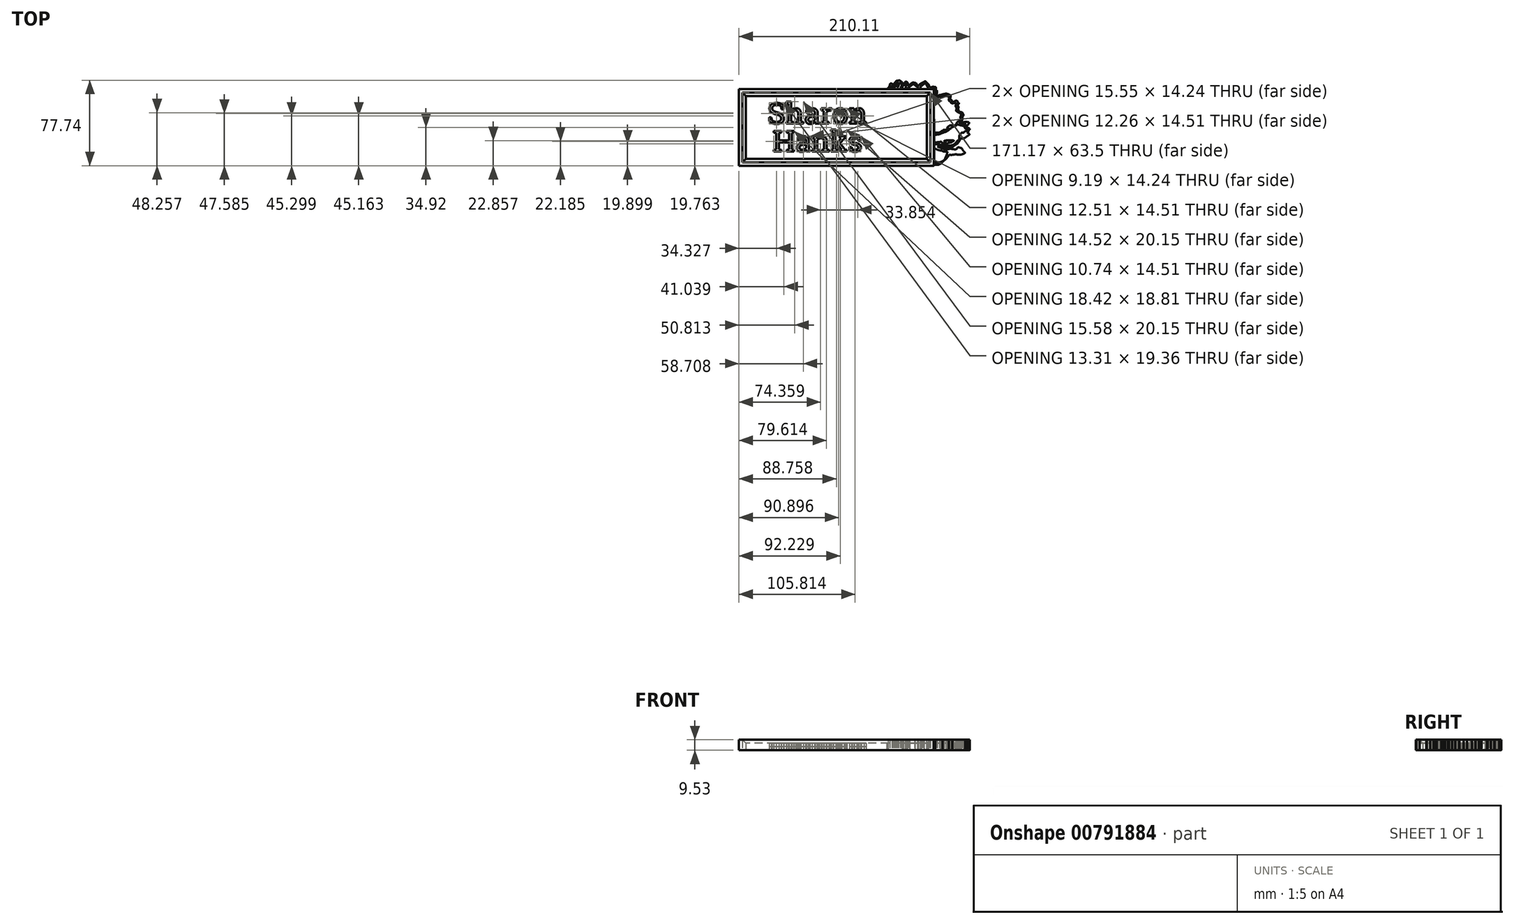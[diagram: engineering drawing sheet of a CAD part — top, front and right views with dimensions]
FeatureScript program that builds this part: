
annotation { "Feature Type Name" : "Feature", "Feature Type Description" : "" }
export const myFeature = defineFeature(function(context is Context, id is Id, definition is map)
    precondition{}
    {
        {
            var Q0;
            Q0=qCreatedBy(makeId("Top.planeOp"),FACE);
            var sketch = newSketch(context, id + "F0", { "sketchPlane" : qUnion([Q0])});
            skText(sketch, "E0", { "text": "Sharon", "fontName": "RobotoSlab-Regular.ttf"});
            skText(sketch, "E1", { "text": "Hanks", "fontName": "RobotoSlab-Regular.ttf"});
            skLineSegment(sketch, "E2.bottom", {"start": v(115.88, 31.75) * mm, "end": v(-55.29, 31.75) * mm});
            skLineSegment(sketch, "E2.top", {"start": v(115.88, -31.75) * mm, "end": v(-55.29, -31.75) * mm});
            skLineSegment(sketch, "E2.left", {"start": v(115.88, 31.75) * mm, "end": v(115.88, -31.75) * mm});
            skPoint(sketch, "E2.middle", {"position": v(0, 0.08) * mm});
            skLineSegment(sketch, "E3", {"start": v(-55.29, 31.75) * mm, "end": v(-55.29, -31.75) * mm});
            skPoint(sketch, "E2.right.start.orphan", {"position": v(-141.56, 31.75) * mm});
            skPoint(sketch, "E4.orphan", {"position": v(-141.56, -31.75) * mm});
            skLineSegment(sketch, "E5.0", {"start": v(112.7, 28.57) * mm, "end": v(-52.11, 28.57) * mm});
            skLineSegment(sketch, "E5.1", {"start": v(112.7, 28.57) * mm, "end": v(112.7, -28.58) * mm});
            skLineSegment(sketch, "E5.2", {"start": v(112.7, -28.57) * mm, "end": v(-52.11, -28.57) * mm});
            skLineSegment(sketch, "E5.3", {"start": v(-52.11, 28.57) * mm, "end": v(-52.11, -28.57) * mm});
            skLineSegment(sketch, "E6.0", {"start": v(-58.46, 34.92) * mm, "end": v(-58.46, -34.92) * mm});
            skLineSegment(sketch, "E6.1", {"start": v(119.06, 34.92) * mm, "end": v(-58.46, 34.92) * mm});
            skLineSegment(sketch, "E6.2", {"start": v(119.06, 34.92) * mm, "end": v(119.06, -34.93) * mm});
            skLineSegment(sketch, "E6.3", {"start": v(119.06, -34.92) * mm, "end": v(-58.46, -34.92) * mm});
            skLineSegment(sketch, "E7", {"start": v(13.4, 3.26) * mm, "end": v(13.4, -3.1) * mm, "construction": true});
            skLineSegment(sketch, "E8", {"start": v(0, 3.26) * mm, "end": v(0, 0.08) * mm, "construction": true});
            skLineSegment(sketch, "E9", {"start": v(0, 0.08) * mm, "end": v(0, -3.1) * mm, "construction": true});
            const initialGuessF0  = {"E0": [-0.03235, 0.00326, 1, 0, 0.01905], "E1": [-0.02755, -0.02214, 1, 0, 0.01905]};
            skSetInitialGuess(sketch, initialGuessF0);
            skSolve(sketch);
        }
        {
            var Q0;
            Q0=qCreatedBy(makeId("Top.planeOp"),FACE);
            var sketch = newSketch(context, id + "F1", { "sketchPlane" : qUnion([Q0])});
            skFitSpline(sketch, "E10", {"points": [v(133.1, 29.85) * mm, v(130.12, 30.6) * mm, v(127, 29.98) * mm, v(124.08, 29.3) * mm]});
            skFitSpline(sketch, "E11", {"points": [v(124.08, 29.3) * mm, v(122.27, 28.6) * mm, v(121.27, 26.77) * mm, v(120.02, 25.45) * mm]});
            skFitSpline(sketch, "E12", {"points": [v(120.02, 25.45) * mm, v(120.68, 28.13) * mm, v(121.7, 30.78) * mm, v(121.7, 33.57) * mm]});
            skFitSpline(sketch, "E13", {"points": [v(121.7, 33.57) * mm, v(120.84, 34.53) * mm, v(120.84, 36.36) * mm, v(119.43, 36.74) * mm]});
            skFitSpline(sketch, "E14", {"points": [v(119.43, 36.74) * mm, v(117.99, 36.9) * mm, v(116.43, 36.39) * mm, v(115.09, 36.42) * mm]});
            skFitSpline(sketch, "E15", {"points": [v(115.09, 36.42) * mm, v(114.61, 38.18) * mm, v(113.57, 39.76) * mm, v(112.17, 40.92) * mm]});
            skFitSpline(sketch, "E16", {"points": [v(112.17, 40.92) * mm, v(111.25, 41.96) * mm, v(109.76, 41.23) * mm, v(108.8, 40.65) * mm]});
            skFitSpline(sketch, "E17", {"points": [v(108.8, 40.65) * mm, v(107.3, 39.96) * mm, v(105.8, 39.03) * mm, v(104.74, 37.77) * mm]});
            skFitSpline(sketch, "E18", {"points": [v(104.74, 37.77) * mm, v(103.8, 38.76) * mm, v(102.95, 40.03) * mm, v(101.6, 40.49) * mm]});
            skFitSpline(sketch, "E19", {"points": [v(101.6, 40.49) * mm, v(99.64, 40.71) * mm, v(97.86, 39.45) * mm, v(96.38, 38.31) * mm]});
            skFitSpline(sketch, "E20", {"points": [v(96.38, 38.31) * mm, v(95.87, 37.63) * mm, v(95.85, 38.65) * mm, v(95.64, 39.03) * mm]});
            skFitSpline(sketch, "E21", {"points": [v(95.64, 39.03) * mm, v(95.32, 39.92) * mm, v(94.9, 40.8) * mm, v(94.24, 41.5) * mm]});
            skFitSpline(sketch, "E22", {"points": [v(94.24, 41.5) * mm, v(92.9, 41.42) * mm, v(92.09, 40.1) * mm, v(90.8, 39.9) * mm]});
            skFitSpline(sketch, "E23", {"points": [v(90.8, 39.9) * mm, v(90.36, 40.74) * mm, v(89.75, 41.48) * mm, v(88.92, 41.95) * mm]});
            skFitSpline(sketch, "E24", {"points": [v(88.92, 41.95) * mm, v(88.27, 42.46) * mm, v(87.29, 42.82) * mm, v(86.56, 42.27) * mm]});
            skFitSpline(sketch, "E25", {"points": [v(86.56, 42.27) * mm, v(85.67, 42.39) * mm, v(84.71, 42.17) * mm, v(84.17, 41.4) * mm]});
            skFitSpline(sketch, "E26", {"points": [v(84.17, 41.4) * mm, v(83.4, 40.64) * mm, v(82.9, 39.3) * mm, v(81.7, 39.22) * mm]});
            skFitSpline(sketch, "E27", {"points": [v(81.7, 39.22) * mm, v(80.83, 39.64) * mm, v(79.34, 39.78) * mm, v(79.01, 38.59) * mm]});
            skFitSpline(sketch, "E28", {"points": [v(79.01, 38.59) * mm, v(77.65, 36.16) * mm, v(75.55, 34.09) * mm, v(74.78, 31.36) * mm]});
            skFitSpline(sketch, "E29", {"points": [v(117.4, -33.94) * mm, v(118.28, -33.58) * mm, v(119.22, -34.2) * mm, v(120.14, -34.05) * mm]});
            skFitSpline(sketch, "E30", {"points": [v(120.14, -34.05) * mm, v(122.64, -34.16) * mm, v(125.12, -33.14) * mm, v(126.87, -31.35) * mm]});
            skFitSpline(sketch, "E31", {"points": [v(126.87, -31.35) * mm, v(129.01, -29.62) * mm, v(131.02, -27.68) * mm, v(132.62, -25.44) * mm]});
            skFitSpline(sketch, "E32", {"points": [v(132.62, -25.44) * mm, v(133.6, -24.98) * mm, v(134.76, -25.17) * mm, v(135.82, -24.96) * mm]});
            skFitSpline(sketch, "E33", {"points": [v(135.82, -24.96) * mm, v(139.4, -24.66) * mm, v(143.14, -24.9) * mm, v(146.6, -23.8) * mm]});
            skFitSpline(sketch, "E34", {"points": [v(146.6, -23.8) * mm, v(147.4, -23.19) * mm, v(146.61, -22.2) * mm, v(146.15, -21.71) * mm]});
            skFitSpline(sketch, "E35", {"points": [v(146.15, -21.71) * mm, v(145.25, -20.58) * mm, v(144.45, -19.1) * mm, v(143.02, -18.6) * mm]});
            skFitSpline(sketch, "E36", {"points": [v(143.02, -18.6) * mm, v(140.95, -18.26) * mm, v(139.21, -20) * mm, v(137.15, -19.9) * mm]});
            skFitSpline(sketch, "E37", {"points": [v(137.15, -19.9) * mm, v(135.72, -19.79) * mm, v(134.3, -19.38) * mm, v(132.84, -19.64) * mm]});
            skFitSpline(sketch, "E38", {"points": [v(132.84, -19.64) * mm, v(131.88, -19.73) * mm, v(130.88, -20.32) * mm, v(130.35, -21.02) * mm]});
            skFitSpline(sketch, "E39", {"points": [v(130.35, -21.02) * mm, v(130.06, -20.36) * mm, v(129.01, -20.32) * mm, v(128.4, -19.94) * mm]});
            skFitSpline(sketch, "E40", {"points": [v(128.4, -19.94) * mm, v(126.35, -19.1) * mm, v(124.28, -18.29) * mm, v(122.2, -17.53) * mm]});
            skFitSpline(sketch, "E41", {"points": [v(122.2, -17.53) * mm, v(127.7, -18.36) * mm, v(133.72, -18.6) * mm, v(138.71, -15.76) * mm]});
            skFitSpline(sketch, "E42", {"points": [v(138.71, -15.76) * mm, v(140.43, -14.83) * mm, v(141.66, -13.3) * mm, v(142.62, -11.64) * mm]});
            skFitSpline(sketch, "E43", {"points": [v(142.62, -11.64) * mm, v(143.08, -10.87) * mm, v(143.73, -10.02) * mm, v(144.73, -10.19) * mm]});
            skFitSpline(sketch, "E44", {"points": [v(144.73, -10.19) * mm, v(146.45, -9.96) * mm, v(147.97, -9) * mm, v(149.42, -8.1) * mm]});
            skFitSpline(sketch, "E45", {"points": [v(149.42, -8.1) * mm, v(150.1, -7.51) * mm, v(151.29, -6.64) * mm, v(150.78, -5.62) * mm]});
            skFitSpline(sketch, "E46", {"points": [v(150.78, -5.62) * mm, v(150.43, -5) * mm, v(149.55, -4.93) * mm, v(149.03, -4.77) * mm]});
            skFitSpline(sketch, "E47", {"points": [v(149.03, -4.77) * mm, v(150.2, -4.1) * mm, v(150.85, -2.84) * mm, v(151.65, -1.8) * mm]});
            skFitSpline(sketch, "E48", {"points": [v(151.65, -1.8) * mm, v(150.89, -0.71) * mm, v(149.29, -0.24) * mm, v(148.9, 1.04) * mm]});
            skFitSpline(sketch, "E49", {"points": [v(148.9, 1.04) * mm, v(149.7, 2.13) * mm, v(150.78, 3.15) * mm, v(150.92, 4.58) * mm]});
            skFitSpline(sketch, "E50", {"points": [v(150.92, 4.58) * mm, v(147.86, 4.98) * mm, v(144.78, 4.41) * mm, v(141.79, 3.8) * mm]});
            skFitSpline(sketch, "E51", {"points": [v(141.79, 3.8) * mm, v(143.36, 5) * mm, v(144.8, 6.6) * mm, v(144.97, 8.66) * mm]});
            skFitSpline(sketch, "E52", {"points": [v(144.97, 8.66) * mm, v(145.22, 9.74) * mm, v(145.9, 10.86) * mm, v(145.65, 11.97) * mm]});
            skFitSpline(sketch, "E53", {"points": [v(145.65, 11.97) * mm, v(144.5, 13.7) * mm, v(142.2, 14.29) * mm, v(141.27, 16.14) * mm]});
            skFitSpline(sketch, "E54", {"points": [v(141.27, 16.14) * mm, v(141.2, 17.28) * mm, v(141.38, 18.49) * mm, v(140.84, 19.54) * mm]});
            skFitSpline(sketch, "E55", {"points": [v(140.84, 19.54) * mm, v(140.86, 20.57) * mm, v(141.84, 21.77) * mm, v(140.98, 22.7) * mm]});
            skFitSpline(sketch, "E56", {"points": [v(140.98, 22.7) * mm, v(139.38, 24.38) * mm, v(136.54, 23.19) * mm, v(134.98, 24.9) * mm]});
            skFitSpline(sketch, "E57", {"points": [v(134.98, 24.9) * mm, v(134, 26.38) * mm, v(134.34, 28.56) * mm, v(133.1, 29.85) * mm]});
            skFitSpline(sketch, "E58", {"points": [v(132.19, 28.2) * mm, v(132.78, 26.61) * mm, v(132.52, 24.62) * mm, v(133.9, 23.38) * mm]});
            skFitSpline(sketch, "E59", {"points": [v(133.9, 23.38) * mm, v(135.47, 21.9) * mm, v(137.87, 22.28) * mm, v(139.75, 21.8) * mm]});
            skFitSpline(sketch, "E60", {"points": [v(139.75, 21.8) * mm, v(139.16, 20.67) * mm, v(138.77, 19.27) * mm, v(139.45, 18.1) * mm]});
            skFitSpline(sketch, "E61", {"points": [v(139.45, 18.1) * mm, v(139.62, 16.83) * mm, v(139.25, 15.12) * mm, v(140.56, 14.31) * mm]});
            skFitSpline(sketch, "E62", {"points": [v(140.56, 14.31) * mm, v(141.75, 13.32) * mm, v(143.56, 12.57) * mm, v(143.73, 10.84) * mm]});
            skFitSpline(sketch, "E63", {"points": [v(143.73, 10.84) * mm, v(143.42, 10.1) * mm, v(143.07, 9.33) * mm, v(143.26, 8.5) * mm]});
            skFitSpline(sketch, "E64", {"points": [v(143.26, 8.5) * mm, v(143.1, 6.78) * mm, v(141.43, 5.74) * mm, v(140.28, 4.66) * mm]});
            skFitSpline(sketch, "E65", {"points": [v(140.28, 4.66) * mm, v(137.68, 1.65) * mm, v(134.6, 1.95) * mm, v(132.02, 0.45) * mm]});
            skFitSpline(sketch, "E66", {"points": [v(132.02, 0.45) * mm, v(131.47, 0.16) * mm, v(131.69, -0.68) * mm, v(132.33, -0.57) * mm]});
            skFitSpline(sketch, "E67", {"points": [v(132.33, -0.57) * mm, v(130.99, -1.38) * mm, v(129.6, -2.35) * mm, v(128, -2.32) * mm]});
            skFitSpline(sketch, "E68", {"points": [v(128, -2.32) * mm, v(127.48, -2.38) * mm, v(127.2, -2.9) * mm, v(127.17, -3.3) * mm]});
            skFitSpline(sketch, "E69", {"points": [v(127.17, -3.3) * mm, v(126.59, -3.22) * mm, v(126.05, -3.36) * mm, v(125.64, -3.78) * mm]});
            skFitSpline(sketch, "E70", {"points": [v(125.64, -3.78) * mm, v(123.63, -4.83) * mm, v(121.29, -4.83) * mm, v(119.1, -5.22) * mm]});
            skFitSpline(sketch, "E71", {"points": [v(93.47, 31.57) * mm, v(93.99, 33.18) * mm, v(94.55, 34.8) * mm, v(94.71, 36.48) * mm]});
            skFitSpline(sketch, "E72", {"points": [v(94.71, 36.48) * mm, v(95.45, 35.62) * mm, v(96.58, 36.46) * mm, v(97.2, 37.02) * mm]});
            skFitSpline(sketch, "E73", {"points": [v(97.2, 37.02) * mm, v(98.42, 38.14) * mm, v(100.4, 39.23) * mm, v(101.97, 38.15) * mm]});
            skFitSpline(sketch, "E74", {"points": [v(101.97, 38.15) * mm, v(102.93, 37.41) * mm, v(103.99, 36.72) * mm, v(104.89, 35.94) * mm]});
            skFitSpline(sketch, "E75", {"points": [v(104.89, 35.94) * mm, v(103.57, 33.95) * mm, v(104.1, 31.23) * mm, v(104, 28.85) * mm]});
            skFitSpline(sketch, "E76", {"points": [v(106.32, 34.05) * mm, v(106.66, 35.4) * mm, v(106.93, 37.09) * mm, v(107.52, 38.25) * mm]});
            skFitSpline(sketch, "E77", {"points": [v(107.52, 38.25) * mm, v(108.5, 38.13) * mm, v(109.1, 39.18) * mm, v(110, 39.37) * mm]});
            skFitSpline(sketch, "E78", {"points": [v(110, 39.37) * mm, v(110.9, 39.85) * mm, v(111.97, 39.45) * mm, v(112.31, 38.5) * mm]});
            skFitSpline(sketch, "E79", {"points": [v(112.31, 38.5) * mm, v(112.97, 37.35) * mm, v(113.7, 36.1) * mm, v(113.9, 34.8) * mm]});
            skFitSpline(sketch, "E80", {"points": [v(117.97, 34.8) * mm, v(118.8, 35.17) * mm, v(119.49, 34.54) * mm, v(119.68, 33.78) * mm]});
            skFitSpline(sketch, "E81", {"points": [v(119.68, 33.78) * mm, v(120.52, 32.03) * mm, v(119.53, 30.1) * mm, v(119.18, 28.34) * mm]});
            skFitSpline(sketch, "E82", {"points": [v(119.18, 28.34) * mm, v(118.38, 25.78) * mm, v(117.7, 23.17) * mm, v(116.48, 20.78) * mm]});
            skFitSpline(sketch, "E83", {"points": [v(118.98, 20.64) * mm, v(119.51, 21.35) * mm, v(119.22, 22.37) * mm, v(120, 22.96) * mm]});
            skFitSpline(sketch, "E84", {"points": [v(120, 22.96) * mm, v(121.51, 24.95) * mm, v(123.01, 27.39) * mm, v(125.66, 27.97) * mm]});
            skFitSpline(sketch, "E85", {"points": [v(125.66, 27.97) * mm, v(127.75, 28.47) * mm, v(129.98, 28.55) * mm, v(132.09, 28.28) * mm]});
            skFitSpline(sketch, "E86", {"points": [v(132.09, 28.28) * mm, v(132.12, 28.26) * mm, v(132.16, 28.23) * mm, v(132.19, 28.2) * mm]});
            skFitSpline(sketch, "E87", {"points": [v(148.3, 2.83) * mm, v(147.81, 2) * mm, v(146.44, 1.33) * mm, v(147, 0.2) * mm]});
            skFitSpline(sketch, "E88", {"points": [v(147, 0.2) * mm, v(147.55, -0.93) * mm, v(149.27, -1.07) * mm, v(149.51, -2.38) * mm]});
            skFitSpline(sketch, "E89", {"points": [v(149.51, -2.38) * mm, v(149.26, -3.12) * mm, v(148.2, -3.14) * mm, v(147.62, -3.58) * mm]});
            skFitSpline(sketch, "E90", {"points": [v(147.62, -3.58) * mm, v(146.93, -3.86) * mm, v(146.44, -4.5) * mm, v(145.94, -4.97) * mm]});
            skFitSpline(sketch, "E91", {"points": [v(145.94, -4.97) * mm, v(145.1, -5) * mm, v(144.05, -5.04) * mm, v(143.6, -5.9) * mm]});
            skFitSpline(sketch, "E92", {"points": [v(143.6, -5.9) * mm, v(142.11, -7.71) * mm, v(142.26, -10.41) * mm, v(140.46, -12.03) * mm]});
            skFitSpline(sketch, "E93", {"points": [v(140.46, -12.03) * mm, v(137.25, -15.6) * mm, v(132.17, -16.68) * mm, v(127.55, -16.34) * mm]});
            skFitSpline(sketch, "E94", {"points": [v(127.55, -16.34) * mm, v(124.91, -16.27) * mm, v(122.33, -15.59) * mm, v(119.71, -15.39) * mm]});
            skFitSpline(sketch, "E95", {"points": [v(119.71, -15.39) * mm, v(119.19, -15.48) * mm, v(118.43, -15.96) * mm, v(118.2, -15.22) * mm]});
            skFitSpline(sketch, "E96", {"points": [v(118.2, -15.22) * mm, v(118.4, -15.05) * mm, v(119.27, -15.24) * mm, v(119.72, -15.23) * mm]});
            skFitSpline(sketch, "E97", {"points": [v(119.72, -15.23) * mm, v(123.5, -15.59) * mm, v(127.5, -16.2) * mm, v(131.13, -14.65) * mm]});
            skFitSpline(sketch, "E98", {"points": [v(131.13, -14.65) * mm, v(132.55, -13.97) * mm, v(134.17, -13.84) * mm, v(135.59, -13.16) * mm]});
            skFitSpline(sketch, "E99", {"points": [v(135.59, -13.16) * mm, v(137.07, -12.08) * mm, v(128.54, -12.34) * mm, v(130.08, -13.35) * mm]});
            skFitSpline(sketch, "E100", {"points": [v(130.08, -13.35) * mm, v(128.72, -13.84) * mm, v(127.23, -14.36) * mm, v(125.82, -14.1) * mm]});
            skFitSpline(sketch, "E101", {"points": [v(125.82, -14.1) * mm, v(126.03, -13.37) * mm, v(125.1, -13.05) * mm, v(124.55, -13.3) * mm]});
            skFitSpline(sketch, "E102", {"points": [v(124.55, -13.3) * mm, v(120.04, -13.7) * mm, v(115.45, -13.1) * mm, v(111.18, -11.61) * mm]});
            skFitSpline(sketch, "E103", {"points": [v(118.55, -7.29) * mm, v(121.2, -6.66) * mm, v(123.95, -6.3) * mm, v(126.45, -5.14) * mm]});
            skFitSpline(sketch, "E104", {"points": [v(126.45, -5.14) * mm, v(130.97, -3.4) * mm, v(134.89, -0.46) * mm, v(139.18, 1.72) * mm]});
            skFitSpline(sketch, "E105", {"points": [v(139.18, 1.72) * mm, v(139.7, 1.85) * mm, v(140.03, 2.33) * mm, v(140.27, 2.7) * mm]});
            skFitSpline(sketch, "E106", {"points": [v(140.27, 2.7) * mm, v(146.58, 1.71) * mm, v(144.51, 3.83) * mm, v(148.3, 2.83) * mm]});
            skFitSpline(sketch, "E107", {"points": [v(93.85, 39.5) * mm, v(94.2, 38.96) * mm, v(94.2, 38.22) * mm, v(93.75, 37.76) * mm]});
            skFitSpline(sketch, "E108", {"points": [v(93.75, 37.76) * mm, v(92.32, 33.29) * mm, v(90.5, 28.72) * mm, v(90.8, 23.93) * mm]});
            skFitSpline(sketch, "E109", {"points": [v(78.28, 20.28) * mm, v(76.97, 25.2) * mm, v(75.6, 33.8) * mm, v(80.9, 37.54) * mm]});
            skFitSpline(sketch, "E110", {"points": [v(80.9, 37.54) * mm, v(82.05, 37.6) * mm, v(80.95, 35.71) * mm, v(82.78, 36.23) * mm]});
            skFitSpline(sketch, "E111", {"points": [v(82.78, 36.23) * mm, v(83.31, 36.47) * mm, v(82.78, 37.43) * mm, v(83.4, 36.93) * mm]});
            skFitSpline(sketch, "E112", {"points": [v(83.4, 36.93) * mm, v(83.92, 36.84) * mm, v(83.15, 38.24) * mm, v(83.82, 38.67) * mm]});
            skFitSpline(sketch, "E113", {"points": [v(83.82, 38.67) * mm, v(84.38, 39.3) * mm, v(84.97, 40) * mm, v(85.66, 40.46) * mm]});
            skFitSpline(sketch, "E114", {"points": [v(85.66, 40.46) * mm, v(86.03, 40.47) * mm, v(87, 39.96) * mm, v(86.26, 39.92) * mm]});
            skFitSpline(sketch, "E115", {"points": [v(86.26, 39.92) * mm, v(85.11, 39.38) * mm, v(85.56, 37.82) * mm, v(86, 36.94) * mm]});
            skFitSpline(sketch, "E116", {"points": [v(86, 36.94) * mm, v(86.18, 36.45) * mm, v(86.55, 37.4) * mm, v(86.72, 37.7) * mm]});
            skFitSpline(sketch, "E117", {"points": [v(86.72, 37.7) * mm, v(87.25, 39.08) * mm, v(88.17, 40.73) * mm, v(88.39, 40.51) * mm]});
            skFitSpline(sketch, "E118", {"points": [v(88.39, 40.51) * mm, v(89.73, 38.64) * mm, v(88.5, 35.3) * mm, v(89.2, 33.4) * mm]});
            skFitSpline(sketch, "E119", {"points": [v(89.2, 33.4) * mm, v(90.53, 34.67) * mm, v(90.24, 36.7) * mm, v(91.31, 38.1) * mm]});
            skFitSpline(sketch, "E120", {"points": [v(91.31, 38.1) * mm, v(92.4, 38.84) * mm, v(92.8, 39.59) * mm, v(93.85, 39.5) * mm]});
            skFitSpline(sketch, "E121", {"points": [v(85.85, -53.41) * mm, v(89.72, -52.45) * mm, v(93.7, -51.78) * mm, v(97.52, -50.6) * mm, v(85.85, -53.41) * mm]});
            skFitSpline(sketch, "E122", {"points": [v(131.02, -24.11) * mm, v(127.38, -30.68) * mm, v(121.3, -32.02) * mm, v(118.15, -32.23) * mm]});
            skFitSpline(sketch, "E123", {"points": [v(114.62, -18.34) * mm, v(119.29, -18.9) * mm, v(122.05, -20.33) * mm, v(126, -21.19) * mm]});
            skFitSpline(sketch, "E124", {"points": [v(126, -21.19) * mm, v(128.79, -22.1) * mm, v(131.08, -22.21) * mm, v(131.02, -24.11) * mm]});
            skLineSegment(sketch, "E125", {"start": v(119.18, -34.86) * mm, "end": v(119.06, 34.93) * mm});
            skLineSegment(sketch, "E126", {"start": v(119.06, 34.93) * mm, "end": v(71.91, 34.93) * mm});
            skSolve(sketch);
        }
        {
            var Q0;
            {var subQ0=sQuery(id+"F1.wireOp",EDGE,"E96");Q0=makeQuery(id+"F1.imprint","IMPRINT",FACE,{"disambiguationData":[TD([[makeQuery(id+"F1.imprint","IMPRINT",EDGE,{"derivedFrom":subQ0}),1.0]])]});}
            var Q1;
            Q1=makeQuery(id+"F1.imprint","IMPRINT",FACE,{"disambiguationData":[TD([[makeQuery(id+"F1.imprint","IMPRINT",EDGE,{"derivedFrom":sQuery(id+"F1.wireOp",EDGE,"E10")}),1.0]])]});
            var Q2;
            Q2=makeQuery(id+"F0.imprint","IMPRINT",FACE,{"disambiguationData":[TD([[makeQuery(id+"F0.imprint","IMPRINT",EDGE,{"derivedFrom":sQuery(id+"F0.wireOp",EDGE,"E2.bottom")}),-1.0]])]});
            extrude(context, id + "F2", {"entities" : qUnion([Q0, Q1, Q2]), "depth" : 9.52 * mm, "offsetDistance" : 25.4 * mm});
        }
        {
            var Q0;
            Q0=makeQuery(id+"F0.imprint","IMPRINT",FACE,{"disambiguationData":[TD([[makeQuery(id+"F0.imprint","IMPRINT",EDGE,{"derivedFrom":sQuery(id+"F0.wireOp",EDGE,"E0.sketch_text.stroke-0")}),1.0]])]});
            var Q1;
            Q1=makeQuery(id+"F0.imprint","IMPRINT",FACE,{"disambiguationData":[TD([[makeQuery(id+"F0.imprint","IMPRINT",EDGE,{"derivedFrom":sQuery(id+"F0.wireOp",EDGE,"E0.sketch_text.stroke-120")}),1.0]])]});
            var Q2;
            Q2=makeQuery(id+"F0.imprint","IMPRINT",FACE,{"disambiguationData":[TD([[makeQuery(id+"F0.imprint","IMPRINT",EDGE,{"derivedFrom":sQuery(id+"F0.wireOp",EDGE,"E0.sketch_text.stroke-83")}),1.0]])]});
            var Q3;
            Q3=makeQuery(id+"F0.imprint","IMPRINT",FACE,{"disambiguationData":[TD([[makeQuery(id+"F0.imprint","IMPRINT",EDGE,{"derivedFrom":sQuery(id+"F0.wireOp",EDGE,"E1.sketch_text.stroke-57")}),1.0]])]});
            var Q4;
            {var subQ1=sQuery(id+"F1.wireOp",EDGE,"E109");Q4=makeQuery(id+"F1.imprint","IMPRINT",FACE,{"disambiguationData":[TD([[makeQuery(id+"F1.imprint","IMPRINT",EDGE,{"derivedFrom":subQ1}),-1.0]])]});}
            var Q5;
            Q5=makeQuery(id+"F1.imprint","IMPRINT",FACE,{"disambiguationData":[TD([[makeQuery(id+"F1.imprint","IMPRINT",EDGE,{"derivedFrom":sQuery(id+"F1.wireOp",EDGE,"E107")}),-1.0]])]});
            var Q6;
            {var subQ1=sQuery(id+"F1.wireOp",EDGE,"E71");Q6=makeQuery(id+"F1.imprint","IMPRINT",FACE,{"disambiguationData":[TD([[makeQuery(id+"F1.imprint","IMPRINT",EDGE,{"derivedFrom":subQ1}),-1.0]])]});}
            var Q7;
            {var subQ4=sQuery(id+"F1.wireOp",EDGE,"E76");Q7=makeQuery(id+"F1.imprint","IMPRINT",FACE,{"disambiguationData":[TD([[makeQuery(id+"F1.imprint","IMPRINT",EDGE,{"derivedFrom":subQ4}),-1.0]])]});}
            var Q8;
            {var subQ0=sQuery(id+"F1.wireOp",EDGE,"E81");Q8=makeQuery(id+"F1.imprint","IMPRINT",FACE,{"disambiguationData":[TD([[makeQuery(id+"F1.imprint","IMPRINT",EDGE,{"derivedFrom":subQ0}),-1.0]])]});}
            var Q9;
            Q9=makeQuery(id+"F1.imprint","IMPRINT",FACE,{"disambiguationData":[TD([[makeQuery(id+"F1.imprint","IMPRINT",EDGE,{"derivedFrom":sQuery(id+"F1.wireOp",EDGE,"E58")}),-1.0]])]});
            var Q10;
            Q10=makeQuery(id+"F1.imprint","IMPRINT",FACE,{"disambiguationData":[TD([[makeQuery(id+"F1.imprint","IMPRINT",EDGE,{"derivedFrom":sQuery(id+"F1.wireOp",EDGE,"E87")}),-1.0]])]});
            var Q11;
            {var subQ0=sQuery(id+"F1.wireOp",EDGE,"E122");Q11=makeQuery(id+"F1.imprint","IMPRINT",FACE,{"disambiguationData":[TD([[makeQuery(id+"F1.imprint","IMPRINT",EDGE,{"derivedFrom":subQ0}),-1.0]])]});}
            extrude(context, id + "F3", {"entities" : qUnion([Q0, Q1, Q2, Q3, Q4, Q5, Q6, Q7, Q8, Q9, Q10, Q11]), "depth" : 6.35 * mm, "offsetDistance" : 25.4 * mm});
        }
        {
            var Q0;
            Q0=makeQuery(id+"F0.imprint","IMPRINT",FACE,{"disambiguationData":[TD([[makeQuery(id+"F0.imprint","IMPRINT",EDGE,{"derivedFrom":sQuery(id+"F0.wireOp",EDGE,"E0.sketch_text.stroke-0")}),-1.0]])]});
            var Q1;
            Q1=makeQuery(id+"F0.imprint","IMPRINT",FACE,{"disambiguationData":[TD([[makeQuery(id+"F0.imprint","IMPRINT",EDGE,{"derivedFrom":sQuery(id+"F0.wireOp",EDGE,"E0.sketch_text.stroke-30")}),-1.0]])]});
            var Q2;
            Q2=makeQuery(id+"F0.imprint","IMPRINT",FACE,{"disambiguationData":[TD([[makeQuery(id+"F0.imprint","IMPRINT",EDGE,{"derivedFrom":sQuery(id+"F0.wireOp",EDGE,"E0.sketch_text.stroke-56")}),-1.0]])]});
            var Q3;
            Q3=makeQuery(id+"F0.imprint","IMPRINT",FACE,{"disambiguationData":[TD([[makeQuery(id+"F0.imprint","IMPRINT",EDGE,{"derivedFrom":sQuery(id+"F0.wireOp",EDGE,"E0.sketch_text.stroke-91")}),-1.0]])]});
            var Q4;
            Q4=makeQuery(id+"F0.imprint","IMPRINT",FACE,{"disambiguationData":[TD([[makeQuery(id+"F0.imprint","IMPRINT",EDGE,{"derivedFrom":sQuery(id+"F0.wireOp",EDGE,"E0.sketch_text.stroke-110")}),-1.0]])]});
            var Q5;
            Q5=makeQuery(id+"F0.imprint","IMPRINT",FACE,{"disambiguationData":[TD([[makeQuery(id+"F0.imprint","IMPRINT",EDGE,{"derivedFrom":sQuery(id+"F0.wireOp",EDGE,"E0.sketch_text.stroke-130")}),-1.0]])]});
            var Q6;
            Q6=makeQuery(id+"F0.imprint","IMPRINT",FACE,{"disambiguationData":[TD([[makeQuery(id+"F0.imprint","IMPRINT",EDGE,{"derivedFrom":sQuery(id+"F0.wireOp",EDGE,"E1.sketch_text.stroke-118")}),-1.0]])]});
            var Q7;
            Q7=makeQuery(id+"F0.imprint","IMPRINT",FACE,{"disambiguationData":[TD([[makeQuery(id+"F0.imprint","IMPRINT",EDGE,{"derivedFrom":sQuery(id+"F0.wireOp",EDGE,"E1.sketch_text.stroke-91")}),-1.0]])]});
            var Q8;
            Q8=makeQuery(id+"F0.imprint","IMPRINT",FACE,{"disambiguationData":[TD([[makeQuery(id+"F0.imprint","IMPRINT",EDGE,{"derivedFrom":sQuery(id+"F0.wireOp",EDGE,"E1.sketch_text.stroke-65")}),-1.0]])]});
            var Q9;
            Q9=makeQuery(id+"F0.imprint","IMPRINT",FACE,{"disambiguationData":[TD([[makeQuery(id+"F0.imprint","IMPRINT",EDGE,{"derivedFrom":sQuery(id+"F0.wireOp",EDGE,"E1.sketch_text.stroke-30")}),-1.0]])]});
            var Q10;
            Q10=makeQuery(id+"F0.imprint","IMPRINT",FACE,{"disambiguationData":[TD([[makeQuery(id+"F0.imprint","IMPRINT",EDGE,{"derivedFrom":sQuery(id+"F0.wireOp",EDGE,"E1.sketch_text.stroke-0")}),-1.0]])]});
            extrude(context, id + "F4", {"entities" : qUnion([Q0, Q1, Q2, Q3, Q4, Q5, Q6, Q7, Q8, Q9, Q10]), "depth" : 3.17 * mm, "offsetDistance" : 25.4 * mm});
        }
        {
            var Q0;
            Q0=makeQuery(id+"F0.imprint","IMPRINT",FACE,{"disambiguationData":[TD([[makeQuery(id+"F0.imprint","IMPRINT",EDGE,{"derivedFrom":sQuery(id+"F0.wireOp",EDGE,"E2.bottom")}),1.0]])]});
            extrude(context, id + "F5", {"entities" : qUnion([Q0]), "depth" : 9.52 * mm, "offsetDistance" : 25.4 * mm});
        }
        {
            var Q0;
            Q0=makeQuery(id+"F5.opExtrude","CAP_EDGE",EDGE,{"disambiguationData":[OSD([sQuery(id+"F0.wireOp",EDGE,"E5.0")])],"isStart":false});
            var Q1;
            Q1=makeQuery(id+"F5.opExtrude","CAP_EDGE",EDGE,{"disambiguationData":[OSD([sQuery(id+"F0.wireOp",EDGE,"E5.3")])],"isStart":false});
            var Q2;
            Q2=makeQuery(id+"F5.opExtrude","CAP_EDGE",EDGE,{"disambiguationData":[OSD([sQuery(id+"F0.wireOp",EDGE,"E5.2")])],"isStart":false});
            var Q3;
            Q3=makeQuery(id+"F5.opExtrude","CAP_EDGE",EDGE,{"disambiguationData":[OSD([sQuery(id+"F0.wireOp",EDGE,"E5.1")])],"isStart":false});
            chamfer(context, id + "F6", {"entities" : qUnion([Q0, Q1, Q2, Q3]), "width" : 3.17 * mm, "tangentPropagation" : true});
        }
    });
